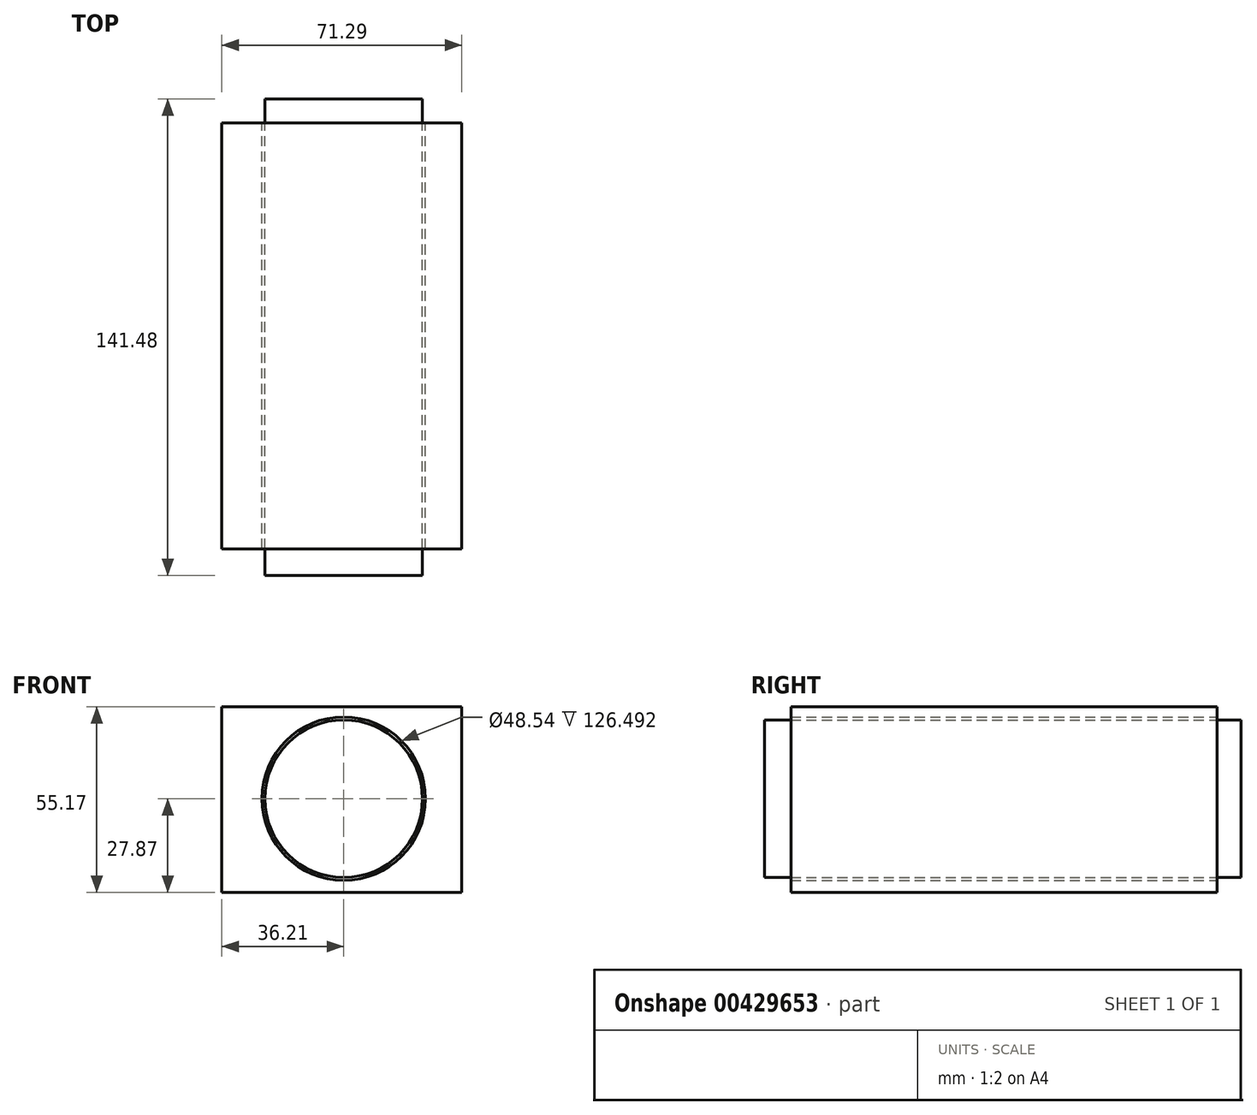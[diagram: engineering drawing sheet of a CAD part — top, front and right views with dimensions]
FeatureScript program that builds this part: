
annotation { "Feature Type Name" : "Feature", "Feature Type Description" : "" }
export const myFeature = defineFeature(function(context is Context, id is Id, definition is map)
    precondition{}
    {
        {
            var Q0;
            Q0=qCreatedBy(makeId("Front.planeOp"),FACE);
            var sketch = newSketch(context, id + "F0", { "sketchPlane" : qUnion([Q0])});
            skLineSegment(sketch, "E0.bottom", {"start": v(-36.21, -27.87) * mm, "end": v(35.08, -27.87) * mm});
            skLineSegment(sketch, "E0.top", {"start": v(-36.21, 27.3) * mm, "end": v(35.08, 27.3) * mm});
            skLineSegment(sketch, "E0.left", {"start": v(-36.21, -27.87) * mm, "end": v(-36.21, 27.3) * mm});
            skLineSegment(sketch, "E0.right", {"start": v(35.08, -27.87) * mm, "end": v(35.08, 27.3) * mm});
            skCircle(sketch, "E1", {"center": v(0, 0) * mm, "radius": 24.27 * mm});
            skSolve(sketch);
        }
        {
            var Q0;
            Q0=makeQuery(id+"F0.imprint","IMPRINT",FACE,{"disambiguationData":[TD([[makeQuery(id+"F0.imprint","IMPRINT",EDGE,{"derivedFrom":sQuery(id+"F0.wireOp",EDGE,"E0.bottom")}),1.0]])]});
            extrude(context, id + "F1", {"entities" : qUnion([Q0]), "depth" : 63.25 * mm, "hasSecondDirection" : true, "secondDirectionOppositeDirection" : true, "secondDirectionDepth" : 63.25 * mm});
        }
        {
            var Q0;
            Q0=qCreatedBy(makeId("Front.planeOp"),FACE);
            var sketch = newSketch(context, id + "F2", { "sketchPlane" : qUnion([Q0])});
            skCircle(sketch, "E2", {"center": v(0, 0) * mm, "radius": 23.4 * mm});
            skSolve(sketch);
        }
        {
            var Q0;
            Q0=makeQuery(id+"F2.imprint","IMPRINT",FACE,{"disambiguationData":[TD([[makeQuery(id+"F2.imprint","IMPRINT",EDGE,{"derivedFrom":sQuery(id+"F2.wireOp",EDGE,"E2")}),1.0]])]});
            extrude(context, id + "F3", {"entities" : qUnion([Q0]), "depth" : 71.12 * mm, "hasSecondDirection" : true, "secondDirectionOppositeDirection" : true, "secondDirectionDepth" : 70.36 * mm});
        }
    });
